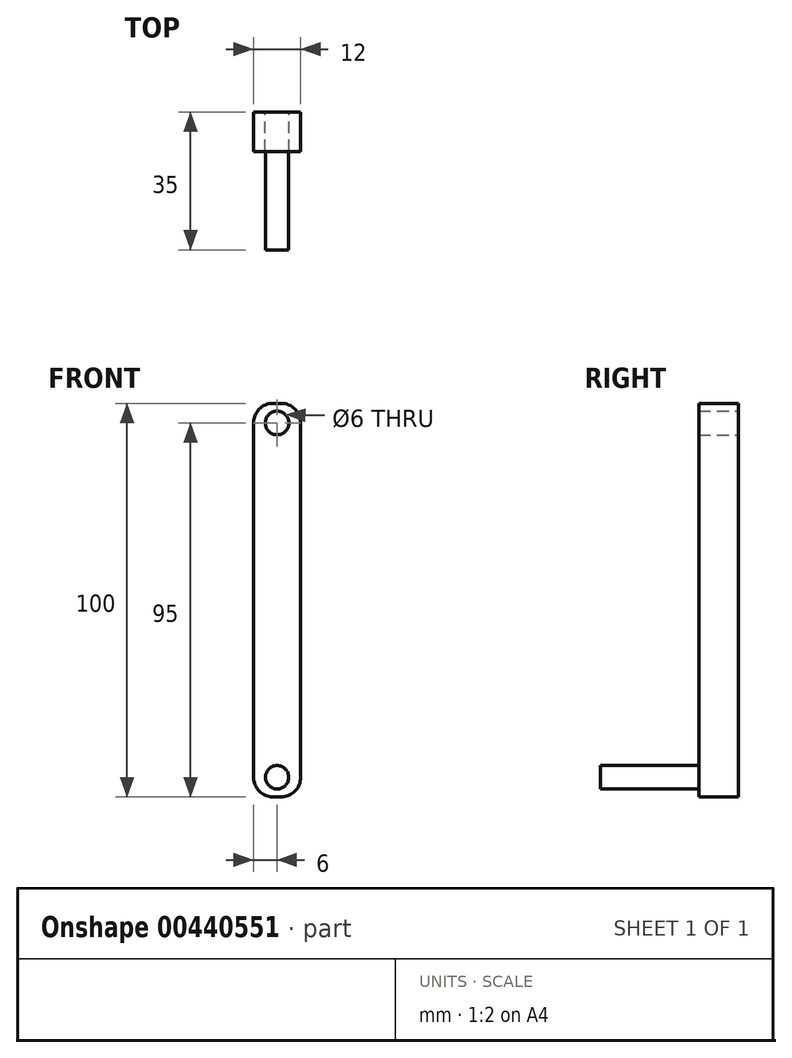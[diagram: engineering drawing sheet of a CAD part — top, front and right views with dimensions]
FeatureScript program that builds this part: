
annotation { "Feature Type Name" : "Feature", "Feature Type Description" : "" }
export const myFeature = defineFeature(function(context is Context, id is Id, definition is map)
    precondition{}
    {
        {
            var Q0;
            Q0=qCreatedBy(makeId("Front.planeOp"),FACE);
            var sketch = newSketch(context, id + "F0", { "sketchPlane" : qUnion([Q0])});
            skLineSegment(sketch, "E0.bottom", {"start": v(-1, 50) * mm, "end": v(1, 50) * mm});
            skLineSegment(sketch, "E0.top", {"start": v(-1, -50) * mm, "end": v(1, -50) * mm});
            skLineSegment(sketch, "E0.left", {"start": v(-6, 45) * mm, "end": v(-6, -45) * mm});
            skLineSegment(sketch, "E0.right", {"start": v(6, 45) * mm, "end": v(6, -45) * mm});
            skPoint(sketch, "E0.middle", {"position": v(0, 0) * mm});
            skPoint(sketch, "E1.visualSharp", {"position": v(-6, 50) * mm});
            skArc(sketch, "E1.filletArc", {"start": v(-1, 50) * mm, "mid": v(-4.54, 48.54) * mm, "end": v(-6, 45) * mm});
            skPoint(sketch, "E2.visualSharp", {"position": v(6, 50) * mm});
            skArc(sketch, "E2.filletArc", {"start": v(6, 45) * mm, "mid": v(4.54, 48.54) * mm, "end": v(1, 50) * mm});
            skLineSegment(sketch, "E3", {"start": v(-1, 45) * mm, "end": v(1, 45) * mm});
            skPoint(sketch, "E4", {"position": v(0, 45) * mm});
            skPoint(sketch, "E5.visualSharp", {"position": v(6, -50) * mm});
            skArc(sketch, "E5.filletArc", {"start": v(1, -50) * mm, "mid": v(4.54, -48.54) * mm, "end": v(6, -45) * mm});
            skPoint(sketch, "E6.visualSharp", {"position": v(-6, -50) * mm});
            skArc(sketch, "E6.filletArc", {"start": v(-6, -45) * mm, "mid": v(-4.54, -48.54) * mm, "end": v(-1, -50) * mm});
            skCircle(sketch, "E7", {"center": v(0, -45) * mm, "radius": 2.97 * mm});
            skSolve(sketch);
        }
        {
            var Q0;
            Q0=makeQuery(id+"F0.imprint","IMPRINT",FACE,{"disambiguationData":[TD([[makeQuery(id+"F0.imprint","IMPRINT",EDGE,{"derivedFrom":sQuery(id+"F0.wireOp",EDGE,"E0.bottom")}),-1.0]])]});
            var Q1;
            Q1=makeQuery(id+"F0.imprint","IMPRINT",FACE,{"disambiguationData":[TD([[makeQuery(id+"F0.imprint","IMPRINT",EDGE,{"derivedFrom":sQuery(id+"F0.wireOp",EDGE,"E7")}),1.0]])]});
            extrude(context, id + "F1", {"entities" : qUnion([Q0, Q1]), "depth" : 10 * mm});
        }
        {
            var Q0;
            Q0=makeQuery(id+"F0.imprint","IMPRINT",FACE,{"disambiguationData":[TD([[makeQuery(id+"F0.imprint","IMPRINT",EDGE,{"derivedFrom":sQuery(id+"F0.wireOp",EDGE,"E7")}),1.0]])]});
            extrude(context, id + "F2", {"entities" : qUnion([Q0]), "operationType" : NewBodyOperationType.ADD, "depth" : 35 * mm});
        }
        {
            var Q0;
            Q0=sQuery(id+"F0.wireOp",VERTEX,"E4");
            var Q1;
            Q1=makeQuery(id+"F1.opExtrude","SWEPT_BODY",BODY,{"disambiguationData":[OSD([sQuery(id+"F0.wireOp",EDGE,"E0.bottom"),sQuery(id+"F0.wireOp",EDGE,"E0.top"),sQuery(id+"F0.wireOp",EDGE,"E0.left"),sQuery(id+"F0.wireOp",EDGE,"E0.right"),sQuery(id+"F0.wireOp",EDGE,"E1.filletArc"),sQuery(id+"F0.wireOp",EDGE,"E2.filletArc"),sQuery(id+"F0.wireOp",EDGE,"E5.filletArc"),sQuery(id+"F0.wireOp",EDGE,"E6.filletArc")])]});
            hole(context, id + "F3", {"style" : HoleStyle.SIMPLE, "endStyle" : HoleEndStyle.THROUGH, "oppositeDirection" : true, "holeDiameter" : 6 * mm, "isTappedThrough" : true, "tappedDepth" : 12 * mm, "tapClearance" : 3, "startFromSketch" : true, "locations" : qUnion([Q0]), "scope" : qUnion([Q1])});
        }
    });
